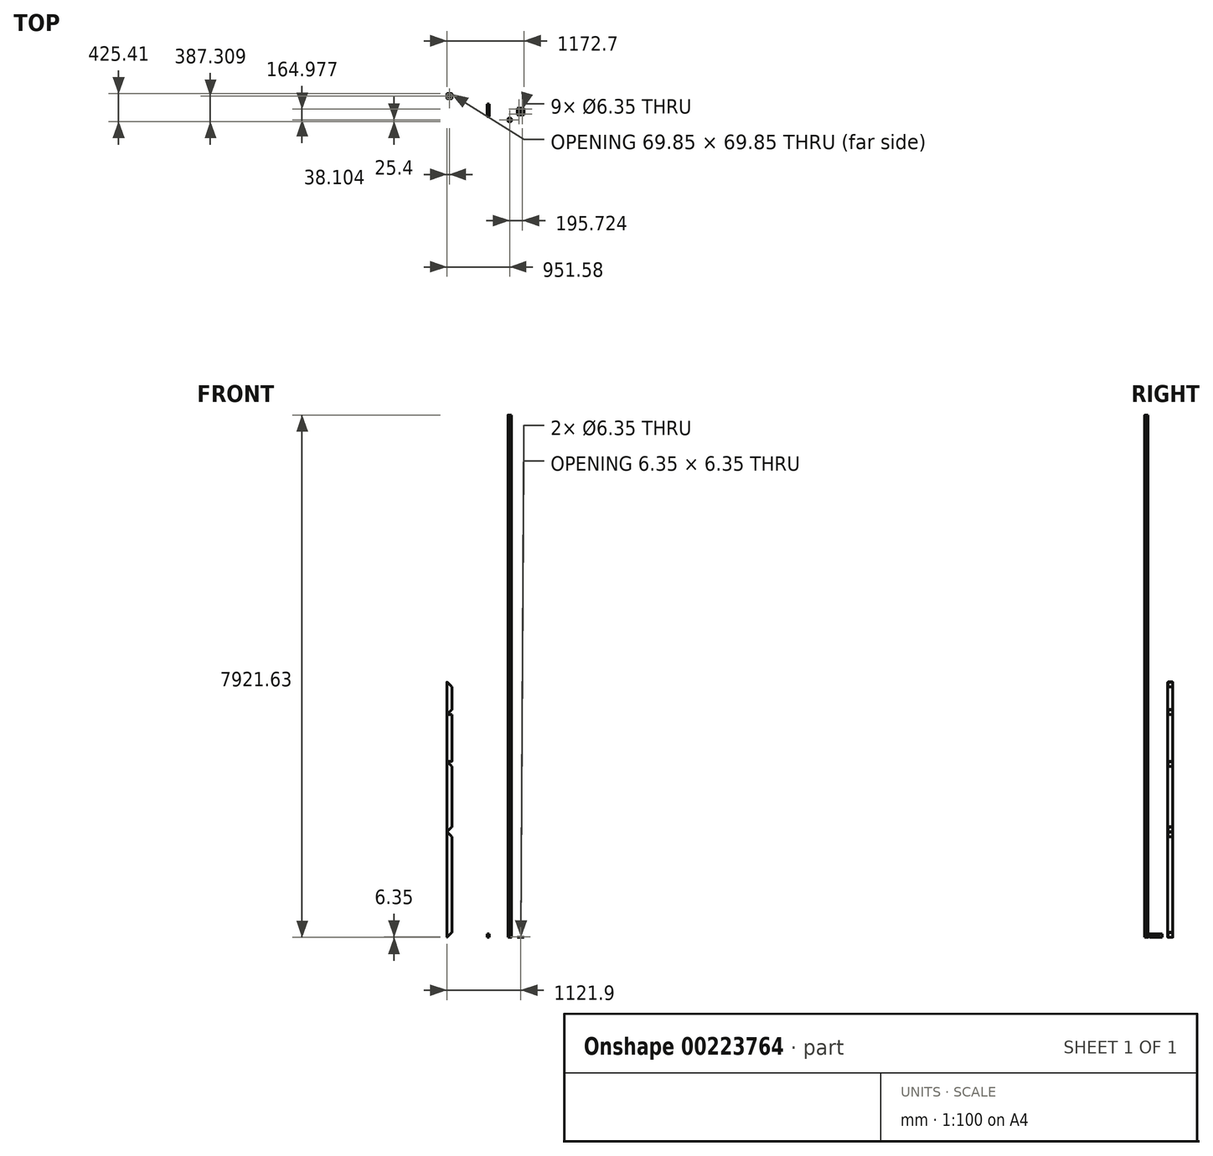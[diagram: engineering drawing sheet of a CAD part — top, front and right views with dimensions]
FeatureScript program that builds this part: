
annotation { "Feature Type Name" : "Feature", "Feature Type Description" : "" }
export const myFeature = defineFeature(function(context is Context, id is Id, definition is map)
    precondition{}
    {
        {
            var Q0;
            Q0=qCreatedBy(makeId("Top.planeOp"),FACE);
            var sketch = newSketch(context, id + "F0", { "sketchPlane" : qUnion([Q0])});
            skLineSegment(sketch, "E0.bottom", {"start": v(25.4, 25.4) * mm, "end": v(-19.05, 25.4) * mm});
            skLineSegment(sketch, "E0.top", {"start": v(25.4, -25.4) * mm, "end": v(-25.4, -25.4) * mm});
            skLineSegment(sketch, "E0.left", {"start": v(25.4, 25.4) * mm, "end": v(25.4, -25.4) * mm});
            skLineSegment(sketch, "E0.right", {"start": v(-25.4, 19.05) * mm, "end": v(-25.4, -25.4) * mm});
            skPoint(sketch, "E0.middle", {"position": v(0, 0) * mm});
            skLineSegment(sketch, "E1", {"start": v(-25.4, 3.18) * mm, "end": v(-20.64, 3.18) * mm});
            skLineSegment(sketch, "E2", {"start": v(-20.64, 3.17) * mm, "end": v(-20.64, 12.7) * mm});
            skLineSegment(sketch, "E3", {"start": v(-20.64, 12.7) * mm, "end": v(-17.2, 12.7) * mm});
            skLineSegment(sketch, "E4", {"start": v(-17.2, 12.7) * mm, "end": v(-7.67, 3.17) * mm});
            skLineSegment(sketch, "E5", {"start": v(-7.67, 3.18) * mm, "end": v(-7.67, 0) * mm});
            skLineSegment(sketch, "E6", {"start": v(-25.4, 25.4) * mm, "end": v(0, 0) * mm, "construction": true});
            skLineSegment(sketch, "E7.MirrorCS", {"start": v(-3.18, 7.67) * mm, "end": v(0, 7.67) * mm});
            skLineSegment(sketch, "E8.MirrorCS", {"start": v(-12.7, 17.2) * mm, "end": v(-3.17, 7.67) * mm});
            skLineSegment(sketch, "E9.MirrorCS", {"start": v(-12.7, 20.64) * mm, "end": v(-12.7, 17.2) * mm});
            skLineSegment(sketch, "E10.MirrorCS", {"start": v(-3.17, 20.64) * mm, "end": v(-12.7, 20.64) * mm});
            skLineSegment(sketch, "E11.MirrorCS", {"start": v(-3.17, 25.4) * mm, "end": v(-3.17, 20.64) * mm});
            skPoint(sketch, "E12.visualSharp", {"position": v(-25.4, 25.4) * mm});
            skArc(sketch, "E12.filletArc", {"start": v(-19.05, 25.4) * mm, "mid": v(-23.54, 23.54) * mm, "end": v(-25.4, 19.05) * mm});
            skCircle(sketch, "E13", {"center": v(0, 0) * mm, "radius": 3.18 * mm});
            skLineSegment(sketch, "E14", {"start": v(-7.67, 0) * mm, "end": v(-3.18, 0) * mm});
            skLineSegment(sketch, "E15", {"start": v(0, 7.67) * mm, "end": v(0, 3.18) * mm});
            skLineSegment(sketch, "E16.1.1", {"start": v(-12.7, -20.64) * mm, "end": v(-12.7, -17.2) * mm});
            skLineSegment(sketch, "E16.1.2", {"start": v(-12.7, -17.2) * mm, "end": v(-3.17, -7.67) * mm});
            skLineSegment(sketch, "E16.1.3", {"start": v(-3.18, -7.67) * mm, "end": v(0, -7.67) * mm});
            skLineSegment(sketch, "E16.1.4", {"start": v(-7.67, -3.17) * mm, "end": v(-7.67, 0) * mm});
            skLineSegment(sketch, "E16.1.5", {"start": v(-25.4, -25.4) * mm, "end": v(0, 0) * mm, "construction": true});
            skLineSegment(sketch, "E16.1.6", {"start": v(-7.67, 0) * mm, "end": v(-3.17, 0) * mm});
            skLineSegment(sketch, "E16.1.7", {"start": v(0, -7.67) * mm, "end": v(0, -3.17) * mm});
            skLineSegment(sketch, "E16.1.8", {"start": v(-3.18, -20.64) * mm, "end": v(-12.7, -20.64) * mm});
            skLineSegment(sketch, "E16.1.9", {"start": v(-17.2, -12.7) * mm, "end": v(-7.67, -3.17) * mm});
            skLineSegment(sketch, "E16.1.10", {"start": v(-20.64, -12.7) * mm, "end": v(-17.2, -12.7) * mm});
            skLineSegment(sketch, "E16.1.11", {"start": v(-3.18, -25.4) * mm, "end": v(-3.18, -20.64) * mm});
            skLineSegment(sketch, "E16.1.12", {"start": v(-20.64, -3.17) * mm, "end": v(-20.64, -12.7) * mm});
            skLineSegment(sketch, "E16.1.13", {"start": v(-25.4, -3.17) * mm, "end": v(-20.64, -3.17) * mm});
            skArc(sketch, "E16.1.14", {"start": v(-25.4, -19.05) * mm, "mid": v(-23.54, -23.54) * mm, "end": v(-19.05, -25.4) * mm});
            skPoint(sketch, "E16.1.15", {"position": v(-25.4, -25.4) * mm});
            skLineSegment(sketch, "E16.2.1", {"start": v(20.64, -12.7) * mm, "end": v(17.2, -12.7) * mm});
            skLineSegment(sketch, "E16.2.2", {"start": v(17.2, -12.7) * mm, "end": v(7.67, -3.17) * mm});
            skLineSegment(sketch, "E16.2.3", {"start": v(7.67, -3.18) * mm, "end": v(7.67, 0) * mm});
            skLineSegment(sketch, "E16.2.4", {"start": v(3.17, -7.67) * mm, "end": v(0, -7.67) * mm});
            skLineSegment(sketch, "E16.2.5", {"start": v(25.4, -25.4) * mm, "end": v(0, 0) * mm, "construction": true});
            skLineSegment(sketch, "E16.2.6", {"start": v(0, -7.67) * mm, "end": v(0, -3.18) * mm});
            skLineSegment(sketch, "E16.2.7", {"start": v(7.67, 0) * mm, "end": v(3.18, 0) * mm});
            skLineSegment(sketch, "E16.2.8", {"start": v(20.64, -3.18) * mm, "end": v(20.64, -12.7) * mm});
            skLineSegment(sketch, "E16.2.9", {"start": v(12.7, -17.2) * mm, "end": v(3.17, -7.67) * mm});
            skLineSegment(sketch, "E16.2.10", {"start": v(12.7, -20.64) * mm, "end": v(12.7, -17.2) * mm});
            skLineSegment(sketch, "E16.2.11", {"start": v(25.4, -3.18) * mm, "end": v(20.64, -3.18) * mm});
            skLineSegment(sketch, "E16.2.12", {"start": v(3.17, -20.64) * mm, "end": v(12.7, -20.64) * mm});
            skLineSegment(sketch, "E16.2.13", {"start": v(3.17, -25.4) * mm, "end": v(3.17, -20.64) * mm});
            skArc(sketch, "E16.2.14", {"start": v(19.05, -25.4) * mm, "mid": v(23.54, -23.54) * mm, "end": v(25.4, -19.05) * mm});
            skPoint(sketch, "E16.2.15", {"position": v(25.4, -25.4) * mm});
            skLineSegment(sketch, "E17.1.3.0", {"start": v(12.7, 20.64) * mm, "end": v(12.7, 17.2) * mm});
            skLineSegment(sketch, "E17.4.3.0", {"start": v(12.7, 17.2) * mm, "end": v(3.18, 7.67) * mm});
            skLineSegment(sketch, "E17.7.3.0", {"start": v(3.18, 7.67) * mm, "end": v(0, 7.67) * mm});
            skLineSegment(sketch, "E17.10.3.0", {"start": v(7.67, 3.17) * mm, "end": v(7.67, 0) * mm});
            skLineSegment(sketch, "E17.13.3.0", {"start": v(25.4, 25.4) * mm, "end": v(0, 0) * mm, "construction": true});
            skLineSegment(sketch, "E17.22.3.0", {"start": v(3.18, 20.64) * mm, "end": v(12.7, 20.64) * mm});
            skLineSegment(sketch, "E17.25.3.0", {"start": v(17.2, 12.7) * mm, "end": v(7.67, 3.17) * mm});
            skLineSegment(sketch, "E17.28.3.0", {"start": v(20.64, 12.7) * mm, "end": v(17.2, 12.7) * mm});
            skLineSegment(sketch, "E17.31.3.0", {"start": v(3.18, 25.4) * mm, "end": v(3.18, 20.64) * mm});
            skLineSegment(sketch, "E17.34.3.0", {"start": v(20.64, 3.17) * mm, "end": v(20.64, 12.7) * mm});
            skLineSegment(sketch, "E17.37.3.0", {"start": v(25.4, 3.17) * mm, "end": v(20.64, 3.17) * mm});
            skArc(sketch, "E17.40.3.0", {"start": v(25.4, 19.05) * mm, "mid": v(23.54, 23.54) * mm, "end": v(19.05, 25.4) * mm});
            skPoint(sketch, "E17.44.3.0", {"position": v(25.4, 25.4) * mm});
            skLineSegment(sketch, "E18.direction1", {"start": v(-25.4, -25.4) * mm, "end": v(38.1, -25.4) * mm, "construction": true});
            skLineSegment(sketch, "E18.direction2", {"start": v(-25.4, -25.4) * mm, "end": v(-25.4, 38.1) * mm, "construction": true});
            skSolve(sketch);
        }
        {
            var Q0;
            Q0=makeQuery(id+"F0.imprint","IMPRINT",FACE,{"disambiguationData":[TD([[makeQuery(id+"F0.imprint","IMPRINT",EDGE,{"derivedFrom":sQuery(id+"F0.wireOp",EDGE,"E17.1.3.0")}),1.0]])]});
            var Q1;
            {var subQ2=sQuery(id+"F0.wireOp",EDGE,"E1");Q1=makeQuery(id+"F0.imprint","IMPRINT",FACE,{"disambiguationData":[TD([[makeQuery(id+"F0.imprint","IMPRINT",EDGE,{"derivedFrom":subQ2}),1.0]])]});}
            var Q2;
            Q2=makeQuery(id+"F0.imprint","IMPRINT",FACE,{"disambiguationData":[TD([[makeQuery(id+"F0.imprint","IMPRINT",EDGE,{"derivedFrom":sQuery(id+"F0.wireOp",EDGE,"E16.1.1")}),1.0]])]});
            var Q3;
            Q3=makeQuery(id+"F0.imprint","IMPRINT",FACE,{"disambiguationData":[TD([[makeQuery(id+"F0.imprint","IMPRINT",EDGE,{"derivedFrom":sQuery(id+"F0.wireOp",EDGE,"E16.2.1")}),1.0]])]});
            extrude(context, id + "F1", {"entities" : qUnion([Q0, Q1, Q2, Q3]), "depth" : 2438.4 * mm});
        }
        {
            var Q0;
            Q0=makeQuery(id+"F1.opExtrude","CAP_FACE",FACE,{"disambiguationData":[OSD([sQuery(id+"F0.wireOp",EDGE,"E0.bottom"),sQuery(id+"F0.wireOp",EDGE,"E0.top"),sQuery(id+"F0.wireOp",EDGE,"E0.left"),sQuery(id+"F0.wireOp",EDGE,"E0.right"),sQuery(id+"F0.wireOp",EDGE,"E1"),sQuery(id+"F0.wireOp",EDGE,"E2"),sQuery(id+"F0.wireOp",EDGE,"E3"),sQuery(id+"F0.wireOp",EDGE,"E4"),sQuery(id+"F0.wireOp",EDGE,"E5"),sQuery(id+"F0.wireOp",EDGE,"E7.MirrorCS"),sQuery(id+"F0.wireOp",EDGE,"E8.MirrorCS"),sQuery(id+"F0.wireOp",EDGE,"E9.MirrorCS"),sQuery(id+"F0.wireOp",EDGE,"E10.MirrorCS"),sQuery(id+"F0.wireOp",EDGE,"E11.MirrorCS"),sQuery(id+"F0.wireOp",EDGE,"E12.filletArc"),sQuery(id+"F0.wireOp",EDGE,"E13"),sQuery(id+"F0.wireOp",EDGE,"E16.1.1"),sQuery(id+"F0.wireOp",EDGE,"E16.1.2"),sQuery(id+"F0.wireOp",EDGE,"E16.1.3"),sQuery(id+"F0.wireOp",EDGE,"E16.1.4"),sQuery(id+"F0.wireOp",EDGE,"E16.1.8"),sQuery(id+"F0.wireOp",EDGE,"E16.1.9"),sQuery(id+"F0.wireOp",EDGE,"E16.1.10"),sQuery(id+"F0.wireOp",EDGE,"E16.1.11"),sQuery(id+"F0.wireOp",EDGE,"E16.1.12"),sQuery(id+"F0.wireOp",EDGE,"E16.1.13"),sQuery(id+"F0.wireOp",EDGE,"E16.1.14"),sQuery(id+"F0.wireOp",EDGE,"E16.2.1"),sQuery(id+"F0.wireOp",EDGE,"E16.2.2"),sQuery(id+"F0.wireOp",EDGE,"E16.2.3"),sQuery(id+"F0.wireOp",EDGE,"E16.2.4"),sQuery(id+"F0.wireOp",EDGE,"E16.2.8"),sQuery(id+"F0.wireOp",EDGE,"E16.2.9"),sQuery(id+"F0.wireOp",EDGE,"E16.2.10"),sQuery(id+"F0.wireOp",EDGE,"E16.2.11"),sQuery(id+"F0.wireOp",EDGE,"E16.2.12"),sQuery(id+"F0.wireOp",EDGE,"E16.2.13"),sQuery(id+"F0.wireOp",EDGE,"E16.2.14"),sQuery(id+"F0.wireOp",EDGE,"E17.1.3.0"),sQuery(id+"F0.wireOp",EDGE,"E17.4.3.0"),sQuery(id+"F0.wireOp",EDGE,"E17.7.3.0"),sQuery(id+"F0.wireOp",EDGE,"E17.10.3.0"),sQuery(id+"F0.wireOp",EDGE,"E17.22.3.0"),sQuery(id+"F0.wireOp",EDGE,"E17.25.3.0"),sQuery(id+"F0.wireOp",EDGE,"E17.28.3.0"),sQuery(id+"F0.wireOp",EDGE,"E17.31.3.0"),sQuery(id+"F0.wireOp",EDGE,"E17.34.3.0"),sQuery(id+"F0.wireOp",EDGE,"E17.37.3.0"),sQuery(id+"F0.wireOp",EDGE,"E17.40.3.0")])],"isStart":false});
            extrude(context, id + "F2", {"entities" : qUnion([Q0]), "depth" : 1981.2 * mm});
        }
        {
            var Q0;
            Q0=makeQuery(id+"F2.opExtrude","CAP_FACE",FACE,{"disambiguationData":[OSD([sQuery(id+"F0.wireOp",EDGE,"E0.bottom"),sQuery(id+"F0.wireOp",EDGE,"E0.top"),sQuery(id+"F0.wireOp",EDGE,"E0.left"),sQuery(id+"F0.wireOp",EDGE,"E0.right"),sQuery(id+"F0.wireOp",EDGE,"E1"),sQuery(id+"F0.wireOp",EDGE,"E2"),sQuery(id+"F0.wireOp",EDGE,"E3"),sQuery(id+"F0.wireOp",EDGE,"E4"),sQuery(id+"F0.wireOp",EDGE,"E5"),sQuery(id+"F0.wireOp",EDGE,"E7.MirrorCS"),sQuery(id+"F0.wireOp",EDGE,"E8.MirrorCS"),sQuery(id+"F0.wireOp",EDGE,"E9.MirrorCS"),sQuery(id+"F0.wireOp",EDGE,"E10.MirrorCS"),sQuery(id+"F0.wireOp",EDGE,"E11.MirrorCS"),sQuery(id+"F0.wireOp",EDGE,"E12.filletArc"),sQuery(id+"F0.wireOp",EDGE,"E13"),sQuery(id+"F0.wireOp",EDGE,"E16.1.1"),sQuery(id+"F0.wireOp",EDGE,"E16.1.2"),sQuery(id+"F0.wireOp",EDGE,"E16.1.3"),sQuery(id+"F0.wireOp",EDGE,"E16.1.4"),sQuery(id+"F0.wireOp",EDGE,"E16.1.8"),sQuery(id+"F0.wireOp",EDGE,"E16.1.9"),sQuery(id+"F0.wireOp",EDGE,"E16.1.10"),sQuery(id+"F0.wireOp",EDGE,"E16.1.11"),sQuery(id+"F0.wireOp",EDGE,"E16.1.12"),sQuery(id+"F0.wireOp",EDGE,"E16.1.13"),sQuery(id+"F0.wireOp",EDGE,"E16.1.14"),sQuery(id+"F0.wireOp",EDGE,"E16.2.1"),sQuery(id+"F0.wireOp",EDGE,"E16.2.2"),sQuery(id+"F0.wireOp",EDGE,"E16.2.3"),sQuery(id+"F0.wireOp",EDGE,"E16.2.4"),sQuery(id+"F0.wireOp",EDGE,"E16.2.8"),sQuery(id+"F0.wireOp",EDGE,"E16.2.9"),sQuery(id+"F0.wireOp",EDGE,"E16.2.10"),sQuery(id+"F0.wireOp",EDGE,"E16.2.11"),sQuery(id+"F0.wireOp",EDGE,"E16.2.12"),sQuery(id+"F0.wireOp",EDGE,"E16.2.13"),sQuery(id+"F0.wireOp",EDGE,"E16.2.14"),sQuery(id+"F0.wireOp",EDGE,"E17.1.3.0"),sQuery(id+"F0.wireOp",EDGE,"E17.4.3.0"),sQuery(id+"F0.wireOp",EDGE,"E17.7.3.0"),sQuery(id+"F0.wireOp",EDGE,"E17.10.3.0"),sQuery(id+"F0.wireOp",EDGE,"E17.22.3.0"),sQuery(id+"F0.wireOp",EDGE,"E17.25.3.0"),sQuery(id+"F0.wireOp",EDGE,"E17.28.3.0"),sQuery(id+"F0.wireOp",EDGE,"E17.31.3.0"),sQuery(id+"F0.wireOp",EDGE,"E17.34.3.0"),sQuery(id+"F0.wireOp",EDGE,"E17.37.3.0"),sQuery(id+"F0.wireOp",EDGE,"E17.40.3.0")])],"isStart":false});
            extrude(context, id + "F3", {"entities" : qUnion([Q0]), "depth" : 406.4 * mm});
        }
        {
            var Q0;
            Q0=qCreatedBy(makeId("Top.planeOp"),FACE);
            var sketch = newSketch(context, id + "F4", { "sketchPlane" : qUnion([Q0])});
            skLineSegment(sketch, "E19.bottom", {"start": v(119.52, 76.08) * mm, "end": v(170.32, 76.08) * mm});
            skLineSegment(sketch, "E19.top", {"start": v(119.52, 177.68) * mm, "end": v(170.32, 177.68) * mm});
            skLineSegment(sketch, "E19.left", {"start": v(119.52, 76.08) * mm, "end": v(119.52, 177.68) * mm});
            skLineSegment(sketch, "E19.right", {"start": v(170.32, 76.08) * mm, "end": v(170.32, 177.68) * mm});
            skCircle(sketch, "E20", {"center": v(144.92, 88.78) * mm, "radius": 3.18 * mm});
            skPoint(sketch, "E20.centerSnap0", {"position": v(144.92, 76.08) * mm});
            skCircle(sketch, "E21", {"center": v(144.92, 164.98) * mm, "radius": 3.18 * mm});
            skSolve(sketch);
        }
        {
            var Q0;
            Q0 = qSketchRegion(id + "F4", true);
            extrude(context, id + "F5", {"entities" : qUnion([Q0]), "depth" : 3.17 * mm});
        }
        {
            var Q0;
            Q0=makeQuery(id+"F5.opExtrude","SWEPT_FACE",FACE,{"disambiguationData":[OSD([sQuery(id+"F4.wireOp",EDGE,"E19.bottom")])]});
            var sketch = newSketch(context, id + "F6", { "sketchPlane" : qUnion([Q0])});
            skCircle(sketch, "E22", {"center": v(170.32, 6.35) * mm, "radius": 3.18 * mm});
            skCircle(sketch, "E23.0", {"center": v(170.32, 6.35) * mm, "radius": 6.35 * mm});
            skSolve(sketch);
        }
        {
            var Q0;
            Q0 = qSketchRegion(id + "F6", true);
            var Q1;
            Q1=makeQuery(id+"F5.opExtrude","SWEPT_FACE",FACE,{"disambiguationData":[OSD([sQuery(id+"F4.wireOp",EDGE,"E19.top")])]});
            extrude(context, id + "F7", {"entities" : qUnion([Q0]), "operationType" : NewBodyOperationType.ADD, "endBound" : BoundingType.UP_TO_SURFACE, "oppositeDirection" : true, "endBoundEntityFace" : qUnion([Q1]), "depth" : 50.8 * mm});
        }
        {
            var Q0;
            Q0=sQuery(id+"F6.wireOp",VERTEX,"E22.center");
            var Q1;
            Q1=qCreatedBy(makeId("Right.planeOp"),FACE);
            cPlane(context, id + "F8", {"entities" : qUnion([Q0, Q1]), "cplaneType" : CPlaneType.PLANE_POINT, "offset" : 25.4 * mm, "width" : 152.4 * mm, "height" : 152.4 * mm});
        }
        {
            var Q0;
            Q0=makeQuery(id+"F5.opExtrude","SWEPT_BODY",BODY,{"disambiguationData":[OSD([sQuery(id+"F4.wireOp",EDGE,"E19.bottom"),sQuery(id+"F4.wireOp",EDGE,"E19.top"),sQuery(id+"F4.wireOp",EDGE,"E19.left"),sQuery(id+"F4.wireOp",EDGE,"E19.right"),sQuery(id+"F4.wireOp",EDGE,"E20"),sQuery(id+"F4.wireOp",EDGE,"E21")])]});
            var Q1;
            Q1=qCreatedBy(id+"F8.planeOp",FACE);
            mirror(context, id + "F9", {"entities" : qUnion([Q0]), "mirrorPlane" : qUnion([Q1])});
        }
        {
            var Q0;
            Q0=makeQuery(id+"F3.opExtrude","CAP_FACE",FACE,{"disambiguationData":[OSD([sQuery(id+"F0.wireOp",EDGE,"E0.bottom"),sQuery(id+"F0.wireOp",EDGE,"E0.top"),sQuery(id+"F0.wireOp",EDGE,"E0.left"),sQuery(id+"F0.wireOp",EDGE,"E0.right"),sQuery(id+"F0.wireOp",EDGE,"E1"),sQuery(id+"F0.wireOp",EDGE,"E2"),sQuery(id+"F0.wireOp",EDGE,"E3"),sQuery(id+"F0.wireOp",EDGE,"E4"),sQuery(id+"F0.wireOp",EDGE,"E5"),sQuery(id+"F0.wireOp",EDGE,"E7.MirrorCS"),sQuery(id+"F0.wireOp",EDGE,"E8.MirrorCS"),sQuery(id+"F0.wireOp",EDGE,"E9.MirrorCS"),sQuery(id+"F0.wireOp",EDGE,"E10.MirrorCS"),sQuery(id+"F0.wireOp",EDGE,"E11.MirrorCS"),sQuery(id+"F0.wireOp",EDGE,"E12.filletArc"),sQuery(id+"F0.wireOp",EDGE,"E13"),sQuery(id+"F0.wireOp",EDGE,"E16.1.1"),sQuery(id+"F0.wireOp",EDGE,"E16.1.2"),sQuery(id+"F0.wireOp",EDGE,"E16.1.3"),sQuery(id+"F0.wireOp",EDGE,"E16.1.4"),sQuery(id+"F0.wireOp",EDGE,"E16.1.8"),sQuery(id+"F0.wireOp",EDGE,"E16.1.9"),sQuery(id+"F0.wireOp",EDGE,"E16.1.10"),sQuery(id+"F0.wireOp",EDGE,"E16.1.11"),sQuery(id+"F0.wireOp",EDGE,"E16.1.12"),sQuery(id+"F0.wireOp",EDGE,"E16.1.13"),sQuery(id+"F0.wireOp",EDGE,"E16.1.14"),sQuery(id+"F0.wireOp",EDGE,"E16.2.1"),sQuery(id+"F0.wireOp",EDGE,"E16.2.2"),sQuery(id+"F0.wireOp",EDGE,"E16.2.3"),sQuery(id+"F0.wireOp",EDGE,"E16.2.4"),sQuery(id+"F0.wireOp",EDGE,"E16.2.8"),sQuery(id+"F0.wireOp",EDGE,"E16.2.9"),sQuery(id+"F0.wireOp",EDGE,"E16.2.10"),sQuery(id+"F0.wireOp",EDGE,"E16.2.11"),sQuery(id+"F0.wireOp",EDGE,"E16.2.12"),sQuery(id+"F0.wireOp",EDGE,"E16.2.13"),sQuery(id+"F0.wireOp",EDGE,"E16.2.14"),sQuery(id+"F0.wireOp",EDGE,"E17.1.3.0"),sQuery(id+"F0.wireOp",EDGE,"E17.4.3.0"),sQuery(id+"F0.wireOp",EDGE,"E17.7.3.0"),sQuery(id+"F0.wireOp",EDGE,"E17.10.3.0"),sQuery(id+"F0.wireOp",EDGE,"E17.22.3.0"),sQuery(id+"F0.wireOp",EDGE,"E17.25.3.0"),sQuery(id+"F0.wireOp",EDGE,"E17.28.3.0"),sQuery(id+"F0.wireOp",EDGE,"E17.31.3.0"),sQuery(id+"F0.wireOp",EDGE,"E17.34.3.0"),sQuery(id+"F0.wireOp",EDGE,"E17.37.3.0"),sQuery(id+"F0.wireOp",EDGE,"E17.40.3.0")])],"isStart":false});
            extrude(context, id + "F10", {"entities" : qUnion([Q0]), "depth" : 1165.22 * mm});
        }
        {
            var Q0;
            Q0=qCreatedBy(makeId("Top.planeOp"),FACE);
            var sketch = newSketch(context, id + "F11", { "sketchPlane" : qUnion([Q0])});
            skLineSegment(sketch, "E24.bottom", {"start": v(-308.94, 50.65) * mm, "end": v(-340.69, 50.65) * mm});
            skLineSegment(sketch, "E24.top", {"start": v(-308.94, 190.35) * mm, "end": v(-340.69, 190.35) * mm});
            skLineSegment(sketch, "E24.left", {"start": v(-308.94, 50.65) * mm, "end": v(-308.94, 190.35) * mm});
            skLineSegment(sketch, "E24.right", {"start": v(-340.69, 50.65) * mm, "end": v(-340.69, 190.35) * mm});
            skSolve(sketch);
        }
        {
            var Q0;
            Q0 = qSketchRegion(id + "F11", true);
            extrude(context, id + "F12", {"entities" : qUnion([Q0]), "depth" : 50.8 * mm});
        }
        {
            var Q0;
            Q0=makeQuery(id+"F12.opExtrude","SWEPT_FACE",FACE,{"disambiguationData":[OSD([sQuery(id+"F11.wireOp",EDGE,"E24.top")])]});
            extrude(context, id + "F13", {"entities" : qUnion([Q0]), "depth" : 50.8 * mm});
        }
        {
            var Q0;
            Q0=makeQuery(id+"F10.opExtrude","CAP_FACE",FACE,{"disambiguationData":[OSD([sQuery(id+"F0.wireOp",EDGE,"E0.bottom"),sQuery(id+"F0.wireOp",EDGE,"E0.top"),sQuery(id+"F0.wireOp",EDGE,"E0.left"),sQuery(id+"F0.wireOp",EDGE,"E0.right"),sQuery(id+"F0.wireOp",EDGE,"E1"),sQuery(id+"F0.wireOp",EDGE,"E2"),sQuery(id+"F0.wireOp",EDGE,"E3"),sQuery(id+"F0.wireOp",EDGE,"E4"),sQuery(id+"F0.wireOp",EDGE,"E5"),sQuery(id+"F0.wireOp",EDGE,"E7.MirrorCS"),sQuery(id+"F0.wireOp",EDGE,"E8.MirrorCS"),sQuery(id+"F0.wireOp",EDGE,"E9.MirrorCS"),sQuery(id+"F0.wireOp",EDGE,"E10.MirrorCS"),sQuery(id+"F0.wireOp",EDGE,"E11.MirrorCS"),sQuery(id+"F0.wireOp",EDGE,"E12.filletArc"),sQuery(id+"F0.wireOp",EDGE,"E13"),sQuery(id+"F0.wireOp",EDGE,"E16.1.1"),sQuery(id+"F0.wireOp",EDGE,"E16.1.2"),sQuery(id+"F0.wireOp",EDGE,"E16.1.3"),sQuery(id+"F0.wireOp",EDGE,"E16.1.4"),sQuery(id+"F0.wireOp",EDGE,"E16.1.8"),sQuery(id+"F0.wireOp",EDGE,"E16.1.9"),sQuery(id+"F0.wireOp",EDGE,"E16.1.10"),sQuery(id+"F0.wireOp",EDGE,"E16.1.11"),sQuery(id+"F0.wireOp",EDGE,"E16.1.12"),sQuery(id+"F0.wireOp",EDGE,"E16.1.13"),sQuery(id+"F0.wireOp",EDGE,"E16.1.14"),sQuery(id+"F0.wireOp",EDGE,"E16.2.1"),sQuery(id+"F0.wireOp",EDGE,"E16.2.2"),sQuery(id+"F0.wireOp",EDGE,"E16.2.3"),sQuery(id+"F0.wireOp",EDGE,"E16.2.4"),sQuery(id+"F0.wireOp",EDGE,"E16.2.8"),sQuery(id+"F0.wireOp",EDGE,"E16.2.9"),sQuery(id+"F0.wireOp",EDGE,"E16.2.10"),sQuery(id+"F0.wireOp",EDGE,"E16.2.11"),sQuery(id+"F0.wireOp",EDGE,"E16.2.12"),sQuery(id+"F0.wireOp",EDGE,"E16.2.13"),sQuery(id+"F0.wireOp",EDGE,"E16.2.14"),sQuery(id+"F0.wireOp",EDGE,"E17.1.3.0"),sQuery(id+"F0.wireOp",EDGE,"E17.4.3.0"),sQuery(id+"F0.wireOp",EDGE,"E17.7.3.0"),sQuery(id+"F0.wireOp",EDGE,"E17.10.3.0"),sQuery(id+"F0.wireOp",EDGE,"E17.22.3.0"),sQuery(id+"F0.wireOp",EDGE,"E17.25.3.0"),sQuery(id+"F0.wireOp",EDGE,"E17.28.3.0"),sQuery(id+"F0.wireOp",EDGE,"E17.31.3.0"),sQuery(id+"F0.wireOp",EDGE,"E17.34.3.0"),sQuery(id+"F0.wireOp",EDGE,"E17.37.3.0"),sQuery(id+"F0.wireOp",EDGE,"E17.40.3.0")])],"isStart":false});
            extrude(context, id + "F14", {"entities" : qUnion([Q0]), "depth" : 1930.4 * mm});
        }
        {
            var Q0;
            Q0=qCreatedBy(makeId("Top.planeOp"),FACE);
            var sketch = newSketch(context, id + "F15", { "sketchPlane" : qUnion([Q0])});
            skLineSegment(sketch, "E25.bottom", {"start": v(-945.23, 400) * mm, "end": v(-881.73, 400) * mm});
            skLineSegment(sketch, "E25.top", {"start": v(-945.23, 323.8) * mm, "end": v(-881.73, 323.8) * mm});
            skLineSegment(sketch, "E25.left", {"start": v(-951.58, 393.66) * mm, "end": v(-951.58, 330.16) * mm});
            skLineSegment(sketch, "E25.right", {"start": v(-875.38, 393.66) * mm, "end": v(-875.38, 330.16) * mm});
            skPoint(sketch, "E26.visualSharp", {"position": v(-951.58, 323.8) * mm});
            skArc(sketch, "E26.filletArc", {"start": v(-951.58, 330.16) * mm, "mid": v(-949.72, 325.67) * mm, "end": v(-945.23, 323.8) * mm});
            skPoint(sketch, "E27.visualSharp", {"position": v(-951.58, 400) * mm});
            skArc(sketch, "E27.filletArc", {"start": v(-945.23, 400) * mm, "mid": v(-949.72, 398.15) * mm, "end": v(-951.58, 393.66) * mm});
            skPoint(sketch, "E28.visualSharp", {"position": v(-875.38, 400) * mm});
            skArc(sketch, "E28.filletArc", {"start": v(-875.38, 393.66) * mm, "mid": v(-877.24, 398.15) * mm, "end": v(-881.73, 400) * mm});
            skPoint(sketch, "E29.visualSharp", {"position": v(-875.38, 323.8) * mm});
            skArc(sketch, "E29.filletArc", {"start": v(-881.73, 323.8) * mm, "mid": v(-877.24, 325.67) * mm, "end": v(-875.38, 330.16) * mm});
            skLineSegment(sketch, "E30.0", {"start": v(-878.55, 393.66) * mm, "end": v(-878.55, 330.16) * mm});
            skArc(sketch, "E30.1", {"start": v(-881.73, 326.98) * mm, "mid": v(-879.48, 327.91) * mm, "end": v(-878.55, 330.16) * mm});
            skArc(sketch, "E30.2", {"start": v(-878.55, 393.66) * mm, "mid": v(-879.48, 395.9) * mm, "end": v(-881.73, 396.83) * mm});
            skLineSegment(sketch, "E30.3", {"start": v(-945.23, 326.98) * mm, "end": v(-881.73, 326.98) * mm});
            skLineSegment(sketch, "E30.4", {"start": v(-945.23, 396.83) * mm, "end": v(-881.73, 396.83) * mm});
            skArc(sketch, "E30.5", {"start": v(-945.23, 396.83) * mm, "mid": v(-947.47, 395.9) * mm, "end": v(-948.4, 393.66) * mm});
            skLineSegment(sketch, "E30.6", {"start": v(-948.4, 393.66) * mm, "end": v(-948.4, 330.16) * mm});
            skArc(sketch, "E30.7", {"start": v(-948.4, 330.16) * mm, "mid": v(-947.47, 327.91) * mm, "end": v(-945.23, 326.98) * mm});
            skSolve(sketch);
        }
        {
            var Q0;
            Q0=makeQuery(id+"F15.imprint","IMPRINT",FACE,{"disambiguationData":[TD([[makeQuery(id+"F15.imprint","IMPRINT",EDGE,{"derivedFrom":sQuery(id+"F15.wireOp",EDGE,"E25.bottom")}),-1.0]])]});
            extrude(context, id + "F16", {"entities" : qUnion([Q0]), "depth" : 1600.2 * mm});
        }
        {
            var Q0;
            Q0=makeQuery(id+"F16.opExtrude","CAP_FACE",FACE,{"disambiguationData":[OSD([sQuery(id+"F15.wireOp",EDGE,"E25.bottom"),sQuery(id+"F15.wireOp",EDGE,"E25.top"),sQuery(id+"F15.wireOp",EDGE,"E25.left"),sQuery(id+"F15.wireOp",EDGE,"E25.right"),sQuery(id+"F15.wireOp",EDGE,"E26.filletArc"),sQuery(id+"F15.wireOp",EDGE,"E27.filletArc"),sQuery(id+"F15.wireOp",EDGE,"E28.filletArc"),sQuery(id+"F15.wireOp",EDGE,"E29.filletArc"),sQuery(id+"F15.wireOp",EDGE,"E30.0"),sQuery(id+"F15.wireOp",EDGE,"E30.1"),sQuery(id+"F15.wireOp",EDGE,"E30.2"),sQuery(id+"F15.wireOp",EDGE,"E30.3"),sQuery(id+"F15.wireOp",EDGE,"E30.4"),sQuery(id+"F15.wireOp",EDGE,"E30.5"),sQuery(id+"F15.wireOp",EDGE,"E30.6"),sQuery(id+"F15.wireOp",EDGE,"E30.7")])],"isStart":false});
            extrude(context, id + "F17", {"entities" : qUnion([Q0]), "depth" : 1066.8 * mm});
        }
        {
            var Q0;
            Q0=makeQuery(id+"F17.opExtrude","CAP_FACE",FACE,{"disambiguationData":[OSD([sQuery(id+"F15.wireOp",EDGE,"E25.bottom"),sQuery(id+"F15.wireOp",EDGE,"E25.top"),sQuery(id+"F15.wireOp",EDGE,"E25.left"),sQuery(id+"F15.wireOp",EDGE,"E25.right"),sQuery(id+"F15.wireOp",EDGE,"E26.filletArc"),sQuery(id+"F15.wireOp",EDGE,"E27.filletArc"),sQuery(id+"F15.wireOp",EDGE,"E28.filletArc"),sQuery(id+"F15.wireOp",EDGE,"E29.filletArc"),sQuery(id+"F15.wireOp",EDGE,"E30.0"),sQuery(id+"F15.wireOp",EDGE,"E30.1"),sQuery(id+"F15.wireOp",EDGE,"E30.2"),sQuery(id+"F15.wireOp",EDGE,"E30.3"),sQuery(id+"F15.wireOp",EDGE,"E30.4"),sQuery(id+"F15.wireOp",EDGE,"E30.5"),sQuery(id+"F15.wireOp",EDGE,"E30.6"),sQuery(id+"F15.wireOp",EDGE,"E30.7")])],"isStart":false});
            extrude(context, id + "F18", {"entities" : qUnion([Q0]), "depth" : 711.2 * mm});
        }
        {
            var Q0;
            Q0=makeQuery(id+"F16.opExtrude","SWEPT_FACE",FACE,{"disambiguationData":[OSD([sQuery(id+"F15.wireOp",EDGE,"E25.bottom")])]});
            var sketch = newSketch(context, id + "F19", { "sketchPlane" : qUnion([Q0])});
            skPoint(sketch, "E31.0", {"position": v(951.58, 0) * mm});
            skLineSegment(sketch, "E32", {"start": v(951.58, 0) * mm, "end": v(861.24, 90.33) * mm});
            skLineSegment(sketch, "E33", {"start": v(861.24, 90.33) * mm, "end": v(861.24, 0) * mm});
            skLineSegment(sketch, "E34", {"start": v(861.24, 0) * mm, "end": v(951.58, 0) * mm});
            skLineSegment(sketch, "E35", {"start": v(881.73, 800.1) * mm, "end": v(1074.61, 800.1) * mm});
            skPoint(sketch, "E35.endSnap0", {"position": v(945.23, 800.1) * mm});
            skPoint(sketch, "E36.MirrorP", {"position": v(951.58, 1600.2) * mm});
            skLineSegment(sketch, "E37.MirrorCS", {"start": v(951.58, 1600.2) * mm, "end": v(861.24, 1509.87) * mm});
            skLineSegment(sketch, "E38.MirrorCS", {"start": v(861.24, 1509.87) * mm, "end": v(861.24, 1600.2) * mm});
            skLineSegment(sketch, "E39.MirrorCS", {"start": v(861.24, 1600.2) * mm, "end": v(951.58, 1600.2) * mm});
            skSolve(sketch);
        }
        {
            var Q0;
            {var subQ0=sQuery(id+"F19.wireOp",EDGE,"E33");Q0=makeQuery(id+"F19.imprint","IMPRINT",FACE,{"disambiguationData":[TD([[makeQuery(id+"F19.imprint","IMPRINT",EDGE,{"derivedFrom":subQ0}),1.0]])]});}
            var Q1;
            {var subQ0=sQuery(id+"F19.wireOp",EDGE,"E32");var subQ1=sQuery(id+"F15.wireOp",EDGE,"E25.bottom");var subQ2=makeQuery(id+"F16.opExtrude","SWEPT_EDGE",EDGE,{"disambiguationData":[OSD([subQ1,sQuery(id+"F15.wireOp",EDGE,"E27.filletArc")])]});var subQ3=makeQuery(id+"F19.imprint","INTERSECT",VERTEX,{"derivedFrom":[subQ2,subQ0]});Q1=makeQuery(id+"F19.imprint","IMPRINT",FACE,{"disambiguationData":[TD([[makeQuery(id+"F19.imprint","IMPRINT",EDGE,{"disambiguationData":[TD([[subQ3,-1.0]])],"derivedFrom":subQ0}),1.0]])]});}
            var Q2;
            {var subQ0=sQuery(id+"F19.wireOp",EDGE,"E34");var subQ1=sQuery(id+"F19.wireOp",EDGE,"E32");var subQ2=makeQuery(id+"F19.imprint","INTERSECT",VERTEX,{"derivedFrom":[subQ1,subQ0]});Q2=makeQuery(id+"F19.imprint","IMPRINT",FACE,{"disambiguationData":[TD([[makeQuery(id+"F19.imprint","IMPRINT",EDGE,{"disambiguationData":[TD([[subQ2,-1.0]])],"derivedFrom":subQ1}),1.0]])]});}
            var Q3;
            {var subQ0=sQuery(id+"F19.wireOp",EDGE,"E37.MirrorCS");var subQ1=sQuery(id+"F15.wireOp",EDGE,"E25.bottom");var subQ2=makeQuery(id+"F16.opExtrude","SWEPT_EDGE",EDGE,{"disambiguationData":[OSD([subQ1,sQuery(id+"F15.wireOp",EDGE,"E27.filletArc")])]});var subQ3=makeQuery(id+"F19.imprint","INTERSECT",VERTEX,{"derivedFrom":[subQ2,subQ0]});Q3=makeQuery(id+"F19.imprint","IMPRINT",FACE,{"disambiguationData":[TD([[makeQuery(id+"F19.imprint","IMPRINT",EDGE,{"disambiguationData":[TD([[subQ3,-1.0]])],"derivedFrom":subQ0}),-1.0]])]});}
            var Q4;
            {var subQ0=sQuery(id+"F19.wireOp",EDGE,"E38.MirrorCS");Q4=makeQuery(id+"F19.imprint","IMPRINT",FACE,{"disambiguationData":[TD([[makeQuery(id+"F19.imprint","IMPRINT",EDGE,{"derivedFrom":subQ0}),-1.0]])]});}
            var Q5;
            {var subQ0=sQuery(id+"F19.wireOp",EDGE,"E39.MirrorCS");var subQ1=sQuery(id+"F19.wireOp",EDGE,"E37.MirrorCS");var subQ2=makeQuery(id+"F19.imprint","INTERSECT",VERTEX,{"derivedFrom":[subQ1,subQ0]});Q5=makeQuery(id+"F19.imprint","IMPRINT",FACE,{"disambiguationData":[TD([[makeQuery(id+"F19.imprint","IMPRINT",EDGE,{"disambiguationData":[TD([[subQ2,-1.0]])],"derivedFrom":subQ1}),-1.0]])]});}
            extrude(context, id + "F20", {"entities" : qUnion([Q0, Q1, Q2, Q3, Q4, Q5]), "operationType" : NewBodyOperationType.REMOVE, "endBound" : BoundingType.THROUGH_ALL, "oppositeDirection" : true, "depth" : 25.4 * mm});
        }
        {
            var Q0;
            Q0=makeQuery(id+"F17.opExtrude","SWEPT_FACE",FACE,{"disambiguationData":[OSD([sQuery(id+"F15.wireOp",EDGE,"E25.bottom")])]});
            var sketch = newSketch(context, id + "F21", { "sketchPlane" : qUnion([Q0])});
            skPoint(sketch, "E40.0", {"position": v(951.58, 1600.2) * mm});
            skLineSegment(sketch, "E41", {"start": v(951.58, 1600.2) * mm, "end": v(849.26, 1702.52) * mm});
            skLineSegment(sketch, "E42", {"start": v(849.26, 1702.52) * mm, "end": v(849.26, 1600.2) * mm});
            skLineSegment(sketch, "E43", {"start": v(849.26, 1600.2) * mm, "end": v(951.58, 1600.2) * mm});
            skLineSegment(sketch, "E44", {"start": v(945.23, 2133.6) * mm, "end": v(817.2, 2133.6) * mm});
            skPoint(sketch, "E45.MirrorP", {"position": v(951.58, 2667) * mm});
            skLineSegment(sketch, "E46.MirrorCS", {"start": v(951.58, 2667) * mm, "end": v(849.26, 2564.68) * mm});
            skLineSegment(sketch, "E47.MirrorCS", {"start": v(849.26, 2564.68) * mm, "end": v(849.26, 2667) * mm});
            skLineSegment(sketch, "E48.MirrorCS", {"start": v(849.26, 2667) * mm, "end": v(951.58, 2667) * mm});
            skSolve(sketch);
        }
        {
            var Q0;
            {var subQ0=sQuery(id+"F21.wireOp",EDGE,"E42");Q0=makeQuery(id+"F21.imprint","IMPRINT",FACE,{"disambiguationData":[TD([[makeQuery(id+"F21.imprint","IMPRINT",EDGE,{"derivedFrom":subQ0}),1.0]])]});}
            var Q1;
            {var subQ0=sQuery(id+"F21.wireOp",EDGE,"E41");var subQ1=sQuery(id+"F15.wireOp",EDGE,"E25.bottom");var subQ2=makeQuery(id+"F17.opExtrude","SWEPT_EDGE",EDGE,{"disambiguationData":[OSD([subQ1,sQuery(id+"F15.wireOp",EDGE,"E27.filletArc")])]});var subQ3=makeQuery(id+"F21.imprint","INTERSECT",VERTEX,{"derivedFrom":[subQ2,subQ0]});Q1=makeQuery(id+"F21.imprint","IMPRINT",FACE,{"disambiguationData":[TD([[makeQuery(id+"F21.imprint","IMPRINT",EDGE,{"disambiguationData":[TD([[subQ3,-1.0]])],"derivedFrom":subQ0}),1.0]])]});}
            var Q2;
            {var subQ0=sQuery(id+"F21.wireOp",EDGE,"E43");var subQ1=sQuery(id+"F21.wireOp",EDGE,"E41");var subQ2=makeQuery(id+"F21.imprint","INTERSECT",VERTEX,{"derivedFrom":[subQ1,subQ0]});Q2=makeQuery(id+"F21.imprint","IMPRINT",FACE,{"disambiguationData":[TD([[makeQuery(id+"F21.imprint","IMPRINT",EDGE,{"disambiguationData":[TD([[subQ2,-1.0]])],"derivedFrom":subQ1}),1.0]])]});}
            var Q3;
            {var subQ0=sQuery(id+"F21.wireOp",EDGE,"E47.MirrorCS");Q3=makeQuery(id+"F21.imprint","IMPRINT",FACE,{"disambiguationData":[TD([[makeQuery(id+"F21.imprint","IMPRINT",EDGE,{"derivedFrom":subQ0}),-1.0]])]});}
            var Q4;
            {var subQ0=sQuery(id+"F21.wireOp",EDGE,"E46.MirrorCS");var subQ1=sQuery(id+"F15.wireOp",EDGE,"E25.bottom");var subQ2=makeQuery(id+"F17.opExtrude","SWEPT_EDGE",EDGE,{"disambiguationData":[OSD([subQ1,sQuery(id+"F15.wireOp",EDGE,"E27.filletArc")])]});var subQ3=makeQuery(id+"F21.imprint","INTERSECT",VERTEX,{"derivedFrom":[subQ2,subQ0]});Q4=makeQuery(id+"F21.imprint","IMPRINT",FACE,{"disambiguationData":[TD([[makeQuery(id+"F21.imprint","IMPRINT",EDGE,{"disambiguationData":[TD([[subQ3,-1.0]])],"derivedFrom":subQ0}),-1.0]])]});}
            var Q5;
            {var subQ0=sQuery(id+"F21.wireOp",EDGE,"E48.MirrorCS");var subQ1=sQuery(id+"F21.wireOp",EDGE,"E46.MirrorCS");var subQ2=makeQuery(id+"F21.imprint","INTERSECT",VERTEX,{"derivedFrom":[subQ1,subQ0]});Q5=makeQuery(id+"F21.imprint","IMPRINT",FACE,{"disambiguationData":[TD([[makeQuery(id+"F21.imprint","IMPRINT",EDGE,{"disambiguationData":[TD([[subQ2,-1.0]])],"derivedFrom":subQ1}),-1.0]])]});}
            extrude(context, id + "F22", {"entities" : qUnion([Q0, Q1, Q2, Q3, Q4, Q5]), "operationType" : NewBodyOperationType.REMOVE, "endBound" : BoundingType.THROUGH_ALL, "oppositeDirection" : true, "depth" : 25.4 * mm});
        }
        {
            var Q0;
            Q0=makeQuery(id+"F18.opExtrude","CAP_FACE",FACE,{"disambiguationData":[OSD([sQuery(id+"F15.wireOp",EDGE,"E25.bottom"),sQuery(id+"F15.wireOp",EDGE,"E25.top"),sQuery(id+"F15.wireOp",EDGE,"E25.left"),sQuery(id+"F15.wireOp",EDGE,"E25.right"),sQuery(id+"F15.wireOp",EDGE,"E26.filletArc"),sQuery(id+"F15.wireOp",EDGE,"E27.filletArc"),sQuery(id+"F15.wireOp",EDGE,"E28.filletArc"),sQuery(id+"F15.wireOp",EDGE,"E29.filletArc"),sQuery(id+"F15.wireOp",EDGE,"E30.0"),sQuery(id+"F15.wireOp",EDGE,"E30.1"),sQuery(id+"F15.wireOp",EDGE,"E30.2"),sQuery(id+"F15.wireOp",EDGE,"E30.3"),sQuery(id+"F15.wireOp",EDGE,"E30.4"),sQuery(id+"F15.wireOp",EDGE,"E30.5"),sQuery(id+"F15.wireOp",EDGE,"E30.6"),sQuery(id+"F15.wireOp",EDGE,"E30.7")])],"isStart":false});
            extrude(context, id + "F23", {"entities" : qUnion([Q0]), "depth" : 495.3 * mm});
        }
        {
            var Q0;
            Q0=makeQuery(id+"F23.opExtrude","SWEPT_FACE",FACE,{"disambiguationData":[OSD([sQuery(id+"F15.wireOp",EDGE,"E25.bottom")])]});
            var sketch = newSketch(context, id + "F24", { "sketchPlane" : qUnion([Q0])});
            skPoint(sketch, "E49.0", {"position": v(951.58, 3378.2) * mm});
            skLineSegment(sketch, "E50", {"start": v(951.58, 3378.2) * mm, "end": v(855.4, 3474.38) * mm});
            skLineSegment(sketch, "E51", {"start": v(855.4, 3474.38) * mm, "end": v(860.88, 3378.2) * mm});
            skLineSegment(sketch, "E52", {"start": v(860.88, 3378.2) * mm, "end": v(951.58, 3378.2) * mm});
            skLineSegment(sketch, "E53", {"start": v(881.73, 3625.85) * mm, "end": v(985.93, 3625.85) * mm});
            skPoint(sketch, "E53.endSnap0", {"position": v(945.23, 3625.85) * mm});
            skPoint(sketch, "E54.MirrorP", {"position": v(951.58, 3873.5) * mm});
            skLineSegment(sketch, "E55.MirrorCS", {"start": v(855.4, 3777.32) * mm, "end": v(860.88, 3873.5) * mm});
            skLineSegment(sketch, "E56.MirrorCS", {"start": v(951.58, 3873.5) * mm, "end": v(855.4, 3777.32) * mm});
            skLineSegment(sketch, "E57.MirrorCS", {"start": v(860.88, 3873.5) * mm, "end": v(951.58, 3873.5) * mm});
            skSolve(sketch);
        }
        {
            var Q0;
            {var subQ0=sQuery(id+"F24.wireOp",EDGE,"E52");var subQ1=sQuery(id+"F24.wireOp",EDGE,"E50");var subQ2=makeQuery(id+"F24.imprint","INTERSECT",VERTEX,{"derivedFrom":[subQ1,subQ0]});Q0=makeQuery(id+"F24.imprint","IMPRINT",FACE,{"disambiguationData":[TD([[makeQuery(id+"F24.imprint","IMPRINT",EDGE,{"disambiguationData":[TD([[subQ2,-1.0]])],"derivedFrom":subQ1}),1.0]])]});}
            var Q1;
            {var subQ0=sQuery(id+"F24.wireOp",EDGE,"E50");var subQ1=sQuery(id+"F15.wireOp",EDGE,"E25.bottom");var subQ2=makeQuery(id+"F23.opExtrude","SWEPT_EDGE",EDGE,{"disambiguationData":[OSD([subQ1,sQuery(id+"F15.wireOp",EDGE,"E27.filletArc")])]});var subQ3=makeQuery(id+"F24.imprint","INTERSECT",VERTEX,{"derivedFrom":[subQ2,subQ0]});Q1=makeQuery(id+"F24.imprint","IMPRINT",FACE,{"disambiguationData":[TD([[makeQuery(id+"F24.imprint","IMPRINT",EDGE,{"disambiguationData":[TD([[subQ3,-1.0]])],"derivedFrom":subQ0}),1.0]])]});}
            var Q2;
            {var subQ0=sQuery(id+"F24.wireOp",EDGE,"E51");Q2=makeQuery(id+"F24.imprint","IMPRINT",FACE,{"disambiguationData":[TD([[makeQuery(id+"F24.imprint","IMPRINT",EDGE,{"derivedFrom":subQ0}),1.0]])]});}
            var Q3;
            {var subQ0=sQuery(id+"F24.wireOp",EDGE,"E55.MirrorCS");Q3=makeQuery(id+"F24.imprint","IMPRINT",FACE,{"disambiguationData":[TD([[makeQuery(id+"F24.imprint","IMPRINT",EDGE,{"derivedFrom":subQ0}),-1.0]])]});}
            var Q4;
            {var subQ0=sQuery(id+"F24.wireOp",EDGE,"E56.MirrorCS");var subQ1=sQuery(id+"F15.wireOp",EDGE,"E25.bottom");var subQ2=makeQuery(id+"F23.opExtrude","SWEPT_EDGE",EDGE,{"disambiguationData":[OSD([subQ1,sQuery(id+"F15.wireOp",EDGE,"E27.filletArc")])]});var subQ3=makeQuery(id+"F24.imprint","INTERSECT",VERTEX,{"derivedFrom":[subQ2,subQ0]});Q4=makeQuery(id+"F24.imprint","IMPRINT",FACE,{"disambiguationData":[TD([[makeQuery(id+"F24.imprint","IMPRINT",EDGE,{"disambiguationData":[TD([[subQ3,-1.0]])],"derivedFrom":subQ0}),-1.0]])]});}
            var Q5;
            {var subQ0=sQuery(id+"F24.wireOp",EDGE,"E57.MirrorCS");var subQ1=sQuery(id+"F24.wireOp",EDGE,"E56.MirrorCS");var subQ2=makeQuery(id+"F24.imprint","INTERSECT",VERTEX,{"derivedFrom":[subQ1,subQ0]});Q5=makeQuery(id+"F24.imprint","IMPRINT",FACE,{"disambiguationData":[TD([[makeQuery(id+"F24.imprint","IMPRINT",EDGE,{"disambiguationData":[TD([[subQ2,-1.0]])],"derivedFrom":subQ1}),-1.0]])]});}
            extrude(context, id + "F25", {"entities" : qUnion([Q0, Q1, Q2, Q3, Q4, Q5]), "operationType" : NewBodyOperationType.REMOVE, "endBound" : BoundingType.THROUGH_ALL, "oppositeDirection" : true, "depth" : 25.4 * mm});
        }
    });
